# Revit family: 6DMLHR-NRG
name_source: partatom
category: Mechanical Equipment
revit_build: Autodesk Revit 2017 (Build: 20171027_0315(x64)
units: mm (PartAtom-declared; Revit-internal decimal feet)

## family parameters
Always vertical = Yes
Cut with Voids When Loaded = No
OmniClass Number = 23.40.40.11.17
OmniClass Title = Refrigerated Cases
Part Type = Normal
Room Calculation Point = No
Round Connector Dimension = Use Radius
Shared = No
Work Plane-Based = Yes

## types (3) — shared parameters
24" Shelf = Yes
BOTTOM ELECTRICAL = Yes
BOTTOM REFRIGERATION PIPING = Yes
BTUH Conventional = 1756
BTUH Parallel = 1500
Certifications = NSF 7, UL471, CSA
DATE = 03/17/2017
DRAIN PIPING = Yes
Default Elevation = 48"
Defrosts Per Day = 6
Description = Rear Load Multi-Deck Merchandiser with Synerg-E™
Discharge Air (°F) = 34 °F
Discharge Air Velocity (FPM) = 200 FPM
EQUIPMENT DESCRIPTION = Rear Load Multi-Deck Merchandiser with Synerg-E™
EQUIPMENT MARK = 6DMLHR-NRG
Evaporator (°F) = 25 °F
GLASS = Glass
Height = 88 5/8"
High Efficiency Amps = 1 A
High Power (Cornice) Amps = 0 A
Item Description = Rear Load Multi-Deck Merchandiser with Synerg-E™
LF STD END = Yes
Legend Number = 6DMLHR-NRG
Manufacturer = HILL PHOENIX
Model = 6DMLHR-NRG
PAINTED METAL UPPER SHELF = PAINTED SHELVES
REAR REFRIGERATION PIPING = Yes
REFRIGERATION PIPING = COPPER PIPE
RT STD END = Yes
Refgn = 8 3/4"
STAINLESS STEEL = GALVANIZED STEEL
Standard Power Amps = 0 A
Superheat Set Point @ Bulb (°F) = 6-8 °F
TOP ELECTRICAL = Yes
TOP REFRIGERATION PIPING = Yes
Timed-Off Defrost Fail-Safe (Min) = 45
Timed-Off Defrost Termination Temp = 47 °F
URL = http://www.hillphoenix.com
Width = 43"

## per-type parameters (varying)
| type | CENTER LINE | DRAIN LINE | Door | High Efficiency Watts | High Power (Cornice) Watts | Length | Length of Cases | Light Length | Lights Per Row | Number of Doors | Number of Fans | Standard Power Watts |
| 08' | 48" | 48" | Door_8 : 08'(Dairy,Deli,Cut Produce) | 65 W | 30 W | 96" | 96" | 4' | 2 | 2 | 3 | 12 W |
| 12' | 72" | 72" | Door_12 : 12'(Dairy,Deli,Cut Produce) | 87 W | 45 W | 144" | 144" | 4' | 3 | 3 | 4 | 18 W |
| 06' | 36" | 36" | Door_6 : 08'(Dairy,Deli,Cut Produce) | 65 W | 24 W | 72" | 72" | 3' | 2 | 3 | 3 | 9 W |

## geometry (parser evidence)
native form markers: Blend x9, Sweep x9
no freeform markers — native parametric forms only
